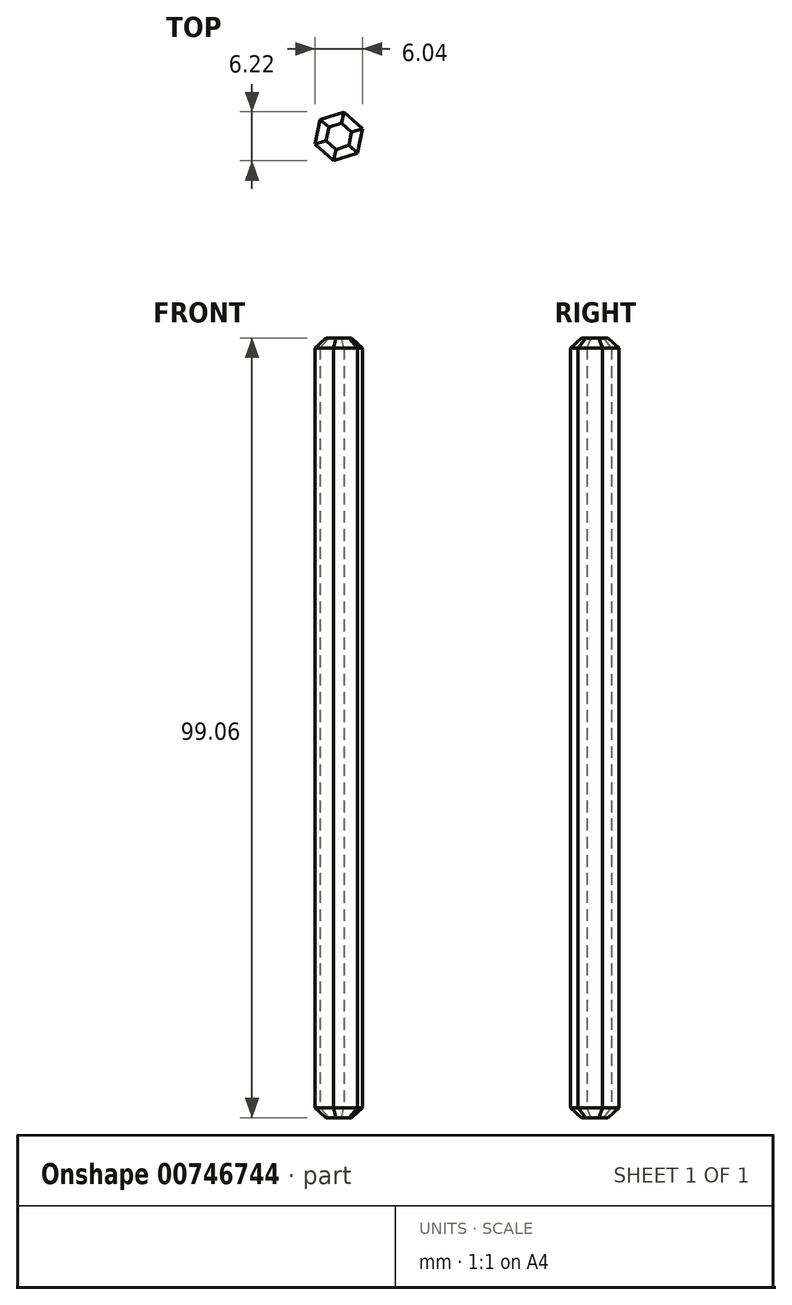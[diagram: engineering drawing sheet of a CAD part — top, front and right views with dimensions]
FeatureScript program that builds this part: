
annotation { "Feature Type Name" : "Feature", "Feature Type Description" : "" }
export const myFeature = defineFeature(function(context is Context, id is Id, definition is map)
    precondition{}
    {
        {
            var Q0;
            Q0=qCreatedBy(makeId("Top.planeOp"),FACE);
            var sketch = newSketch(context, id + "F0", { "sketchPlane" : qUnion([Q0])});
            skCircle(sketch, "E0.cCircle", {"center": v(-41.05, 33.2) * mm, "radius": 3.18 * mm, "construction": true});
            skLineSegment(sketch, "E0.0", {"start": v(-38.69, 31.07) * mm, "end": v(-41.71, 30.1) * mm});
            skLineSegment(sketch, "E0.1", {"start": v(-41.71, 30.1) * mm, "end": v(-44.07, 32.22) * mm});
            skLineSegment(sketch, "E0.2", {"start": v(-44.07, 32.22) * mm, "end": v(-43.4, 35.33) * mm});
            skLineSegment(sketch, "E0.3", {"start": v(-43.4, 35.33) * mm, "end": v(-40.38, 36.3) * mm});
            skLineSegment(sketch, "E0.4", {"start": v(-40.38, 36.3) * mm, "end": v(-38.03, 34.18) * mm});
            skLineSegment(sketch, "E0.5", {"start": v(-38.03, 34.18) * mm, "end": v(-38.69, 31.07) * mm});
            skSolve(sketch);
        }
        {
            var Q0;
            Q0=makeQuery(id+"F0.imprint","IMPRINT",FACE,{"disambiguationData":[TD([[makeQuery(id+"F0.imprint","IMPRINT",EDGE,{"derivedFrom":sQuery(id+"F0.wireOp",EDGE,"E0.0")}),-1.0]])]});
            extrude(context, id + "F1", {"entities" : qUnion([Q0]), "depth" : 99.06 * mm, "offsetDistance" : 25.4 * mm});
        }
        {
            var Q0;
            Q0=makeQuery(id+"F1.opExtrude","CAP_FACE",FACE,{"disambiguationData":[OSD([sQuery(id+"F0.wireOp",EDGE,"E0.0"),sQuery(id+"F0.wireOp",EDGE,"E0.1"),sQuery(id+"F0.wireOp",EDGE,"E0.2"),sQuery(id+"F0.wireOp",EDGE,"E0.3"),sQuery(id+"F0.wireOp",EDGE,"E0.4"),sQuery(id+"F0.wireOp",EDGE,"E0.5")])],"isStart":true});
            chamfer(context, id + "F2", {"entities" : qUnion([Q0]), "width" : 1.27 * mm, "tangentPropagation" : true});
        }
        {
            var Q0;
            Q0=makeQuery(id+"F1.opExtrude","CAP_FACE",FACE,{"disambiguationData":[OSD([sQuery(id+"F0.wireOp",EDGE,"E0.0"),sQuery(id+"F0.wireOp",EDGE,"E0.1"),sQuery(id+"F0.wireOp",EDGE,"E0.2"),sQuery(id+"F0.wireOp",EDGE,"E0.3"),sQuery(id+"F0.wireOp",EDGE,"E0.4"),sQuery(id+"F0.wireOp",EDGE,"E0.5")])],"isStart":false});
            chamfer(context, id + "F3", {"entities" : qUnion([Q0]), "width" : 1.27 * mm, "tangentPropagation" : true});
        }
    });
